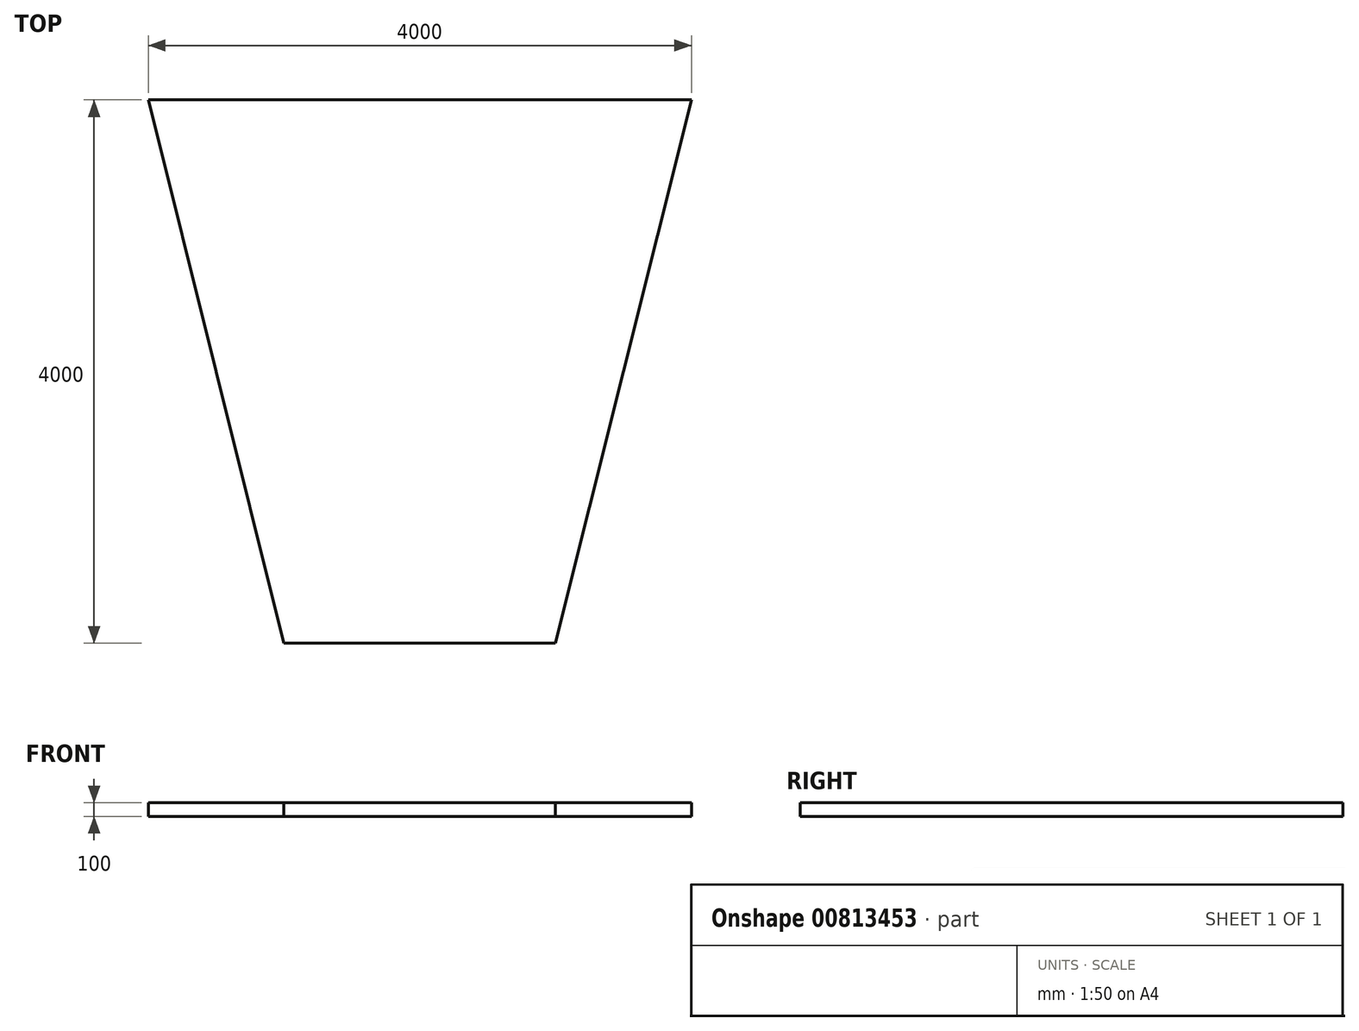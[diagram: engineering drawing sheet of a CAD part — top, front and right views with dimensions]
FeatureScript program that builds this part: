
annotation { "Feature Type Name" : "Feature", "Feature Type Description" : "" }
export const myFeature = defineFeature(function(context is Context, id is Id, definition is map)
    precondition{}
    {
        {
            var Q0;
            Q0=qCreatedBy(makeId("Top.planeOp"),FACE);
            var sketch = newSketch(context, id + "F0", { "sketchPlane" : qUnion([Q0])});
            skLineSegment(sketch, "E0", {"start": v(-1998.12, 2653.05) * mm, "end": v(2001.88, 2653.05) * mm});
            skLineSegment(sketch, "E1", {"start": v(0, -1346.95) * mm, "end": v(-1000, -1346.95) * mm});
            skLineSegment(sketch, "E2.MirrorCS", {"start": v(0, -1346.95) * mm, "end": v(1000, -1346.95) * mm});
            skLineSegment(sketch, "E3", {"start": v(1000, -1346.95) * mm, "end": v(2001.88, 2653.05) * mm});
            skLineSegment(sketch, "E4", {"start": v(-1000, -1346.95) * mm, "end": v(-1998.12, 2653.05) * mm});
            skSolve(sketch);
        }
        {
            var Q0;
            Q0=makeQuery(id+"F0.imprint","IMPRINT",FACE,{"disambiguationData":[TD([[makeQuery(id+"F0.imprint","IMPRINT",EDGE,{"derivedFrom":sQuery(id+"F0.wireOp",EDGE,"E0")}),-1.0]])]});
            extrude(context, id + "F1", {"entities" : qUnion([Q0]), "depth" : 100 * mm, "offsetDistance" : 25 * mm});
        }
    });
